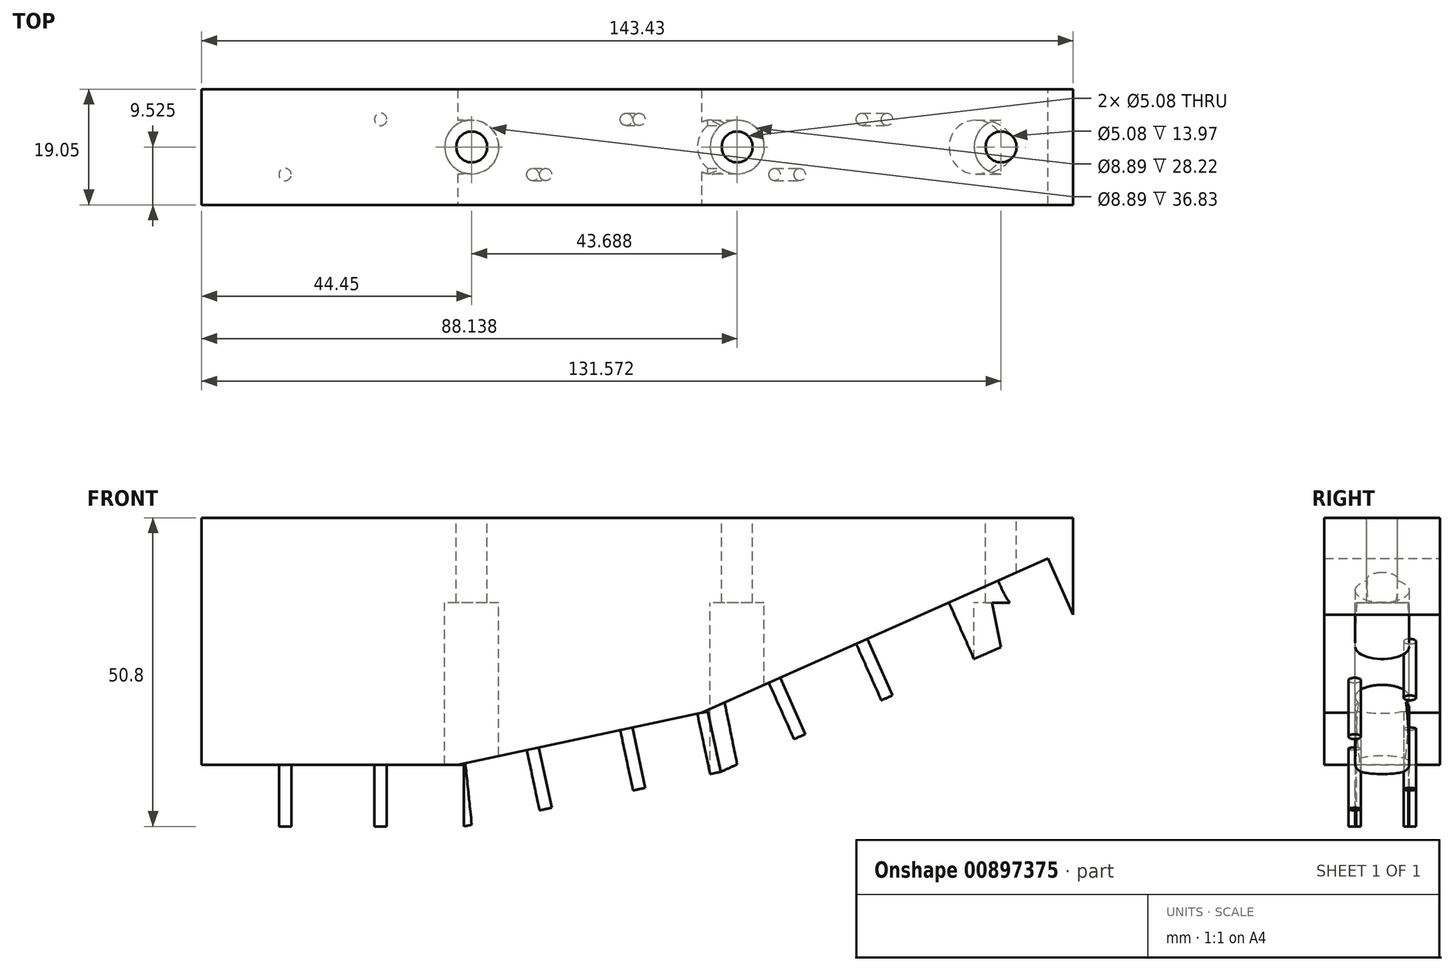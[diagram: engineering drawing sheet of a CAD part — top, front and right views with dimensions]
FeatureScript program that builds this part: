
annotation { "Feature Type Name" : "Feature", "Feature Type Description" : "" }
export const myFeature = defineFeature(function(context is Context, id is Id, definition is map)
    precondition{}
    {
        {
            var Q0;
            Q0=qCreatedBy(makeId("Front.planeOp"),FACE);
            var sketch = newSketch(context, id + "F0", { "sketchPlane" : qUnion([Q0])});
            skLineSegment(sketch, "E0.left", {"start": v(6.35, 57.15) * mm, "end": v(6.35, 6.35) * mm});
            skLineSegment(sketch, "E1", {"start": v(6.35, 6.35) * mm, "end": v(49.53, 6.35) * mm});
            skLineSegment(sketch, "E2", {"start": v(49.53, 6.35) * mm, "end": v(91.77, 15.33) * mm});
            skLineSegment(sketch, "E3", {"start": v(91.77, 15.33) * mm, "end": v(149.78, 41.16) * mm});
            skLineSegment(sketch, "E4", {"start": v(149.78, 41.16) * mm, "end": v(149.78, 57.15) * mm});
            skLineSegment(sketch, "E5", {"start": v(6.35, 57.15) * mm, "end": v(149.8, 57.15) * mm});
            skSolve(sketch);
        }
        {
            var Q0;
            {var subQ0=sQuery(id+"F0.wireOp",EDGE,"E0.left");Q0=makeQuery(id+"F0.imprint","IMPRINT",FACE,{"disambiguationData":[TD([[makeQuery(id+"F0.imprint","IMPRINT",EDGE,{"derivedFrom":subQ0}),1.0]])]});}
            extrude(context, id + "F1", {"entities" : qUnion([Q0]), "depth" : 19.05 * mm, "offsetDistance" : 25.4 * mm});
        }
        {
            var Q0;
            Q0=makeQuery(id+"F1.opExtrude","SWEPT_FACE",FACE,{"disambiguationData":[OSD([sQuery(id+"F0.wireOp",EDGE,"E5")])]});
            var sketch = newSketch(context, id + "F2", { "sketchPlane" : qUnion([Q0])});
            skLineSegment(sketch, "E6", {"start": v(50.8, 21.95) * mm, "end": v(50.8, -45.54) * mm, "construction": true});
            skLineSegment(sketch, "E7", {"start": v(94.49, 24.88) * mm, "end": v(94.49, -40.3) * mm, "construction": true});
            skLineSegment(sketch, "E8", {"start": v(137.92, 28.66) * mm, "end": v(137.92, -40.3) * mm, "construction": true});
            skLineSegment(sketch, "E9", {"start": v(-7.3, -9.53) * mm, "end": v(174, -9.53) * mm, "construction": true});
            skPoint(sketch, "E9.startSnap0", {"position": v(6.35, -9.53) * mm});
            skCircle(sketch, "E10", {"center": v(50.8, -9.53) * mm, "radius": 4.45 * mm});
            skCircle(sketch, "E11", {"center": v(94.49, -9.53) * mm, "radius": 4.45 * mm});
            skCircle(sketch, "E12", {"center": v(137.92, -9.53) * mm, "radius": 4.45 * mm});
            skCircle(sketch, "E13", {"center": v(50.8, -9.53) * mm, "radius": 2.54 * mm});
            skCircle(sketch, "E14", {"center": v(94.49, -9.53) * mm, "radius": 2.54 * mm});
            skCircle(sketch, "E15", {"center": v(137.92, -9.53) * mm, "radius": 2.54 * mm});
            skSolve(sketch);
        }
        {
            var Q0;
            Q0=makeQuery(id+"F2.imprint","IMPRINT",FACE,{"disambiguationData":[TD([[makeQuery(id+"F2.imprint","IMPRINT",EDGE,{"derivedFrom":sQuery(id+"F2.wireOp",EDGE,"E13")}),1.0]])]});
            var Q1;
            Q1=makeQuery(id+"F2.imprint","IMPRINT",FACE,{"disambiguationData":[TD([[makeQuery(id+"F2.imprint","IMPRINT",EDGE,{"derivedFrom":sQuery(id+"F2.wireOp",EDGE,"E14")}),1.0]])]});
            var Q2;
            Q2=makeQuery(id+"F2.imprint","IMPRINT",FACE,{"disambiguationData":[TD([[makeQuery(id+"F2.imprint","IMPRINT",EDGE,{"derivedFrom":sQuery(id+"F2.wireOp",EDGE,"E15")}),1.0]])]});
            extrude(context, id + "F3", {"entities" : qUnion([Q0, Q1, Q2]), "operationType" : NewBodyOperationType.REMOVE, "endBound" : BoundingType.THROUGH_ALL, "oppositeDirection" : true, "depth" : 25.4 * mm, "offsetDistance" : 25.4 * mm});
        }
        {
            var Q0;
            Q0=makeQuery(id+"F2.imprint","IMPRINT",FACE,{"disambiguationData":[TD([[makeQuery(id+"F2.imprint","IMPRINT",EDGE,{"derivedFrom":sQuery(id+"F2.wireOp",EDGE,"E10")}),1.0]])]});
            var Q1;
            Q1=makeQuery(id+"F2.imprint","IMPRINT",FACE,{"disambiguationData":[TD([[makeQuery(id+"F2.imprint","IMPRINT",EDGE,{"derivedFrom":sQuery(id+"F2.wireOp",EDGE,"E11")}),1.0]])]});
            var Q2;
            Q2=makeQuery(id+"F2.imprint","IMPRINT",FACE,{"disambiguationData":[TD([[makeQuery(id+"F2.imprint","IMPRINT",EDGE,{"derivedFrom":sQuery(id+"F2.wireOp",EDGE,"E12")}),1.0]])]});
            extrude(context, id + "F4", {"entities" : qUnion([Q0, Q1, Q2]), "operationType" : NewBodyOperationType.REMOVE, "oppositeDirection" : true, "depth" : 54.36 * mm, "offsetDistance" : 25.4 * mm, "hasSecondDirection" : true, "secondDirectionOppositeDirection" : true, "secondDirectionDepth" : 13.97 * mm});
        }
        {
            var Q0;
            Q0=makeQuery(id+"F1.opExtrude","SWEPT_FACE",FACE,{"disambiguationData":[OSD([sQuery(id+"F0.wireOp",EDGE,"E1")])]});
            var sketch = newSketch(context, id + "F5", { "sketchPlane" : qUnion([Q0])});
            skLineSegment(sketch, "E16", {"start": v(27.94, 21.39) * mm, "end": v(27.94, -3.77) * mm, "construction": true});
            skPoint(sketch, "E16.startSnap0", {"position": v(27.94, 19.05) * mm});
            skLineSegment(sketch, "E17", {"start": v(2.63, 9.53) * mm, "end": v(172.55, 9.53) * mm, "construction": true});
            skPoint(sketch, "E17.startSnap0", {"position": v(6.35, 9.53) * mm});
            skCircle(sketch, "E18", {"center": v(27.94, 9.53) * mm, "radius": 9.08 * mm});
            skLineSegment(sketch, "E19", {"start": v(27.94, -11.85) * mm, "end": v(27.94, 27.97) * mm, "construction": true});
            skLineSegment(sketch, "E20", {"start": v(5.3, 9.53) * mm, "end": v(51, 9.53) * mm, "construction": true});
            skLineSegment(sketch, "E21", {"start": v(20.08, 14.07) * mm, "end": v(50.17, -3.3) * mm, "construction": true});
            skCircle(sketch, "E22", {"center": v(20.08, 14.07) * mm, "radius": 1.02 * mm});
            skCircle(sketch, "E23", {"center": v(35.8, 4.98) * mm, "radius": 1.02 * mm});
            skSolve(sketch);
        }
        {
            var Q0;
            {var subQ0=sQuery(id+"F5.wireOp",EDGE,"E22");var subQ1=sQuery(id+"F5.wireOp",EDGE,"E18");var subQ2=makeQuery(id+"F5.imprint","INTERSECT",VERTEX,{"disambiguationData":[OD(0.0)],"derivedFrom":[subQ1,subQ0]});Q0=makeQuery(id+"F5.imprint","IMPRINT",FACE,{"disambiguationData":[TD([[makeQuery(id+"F5.imprint","IMPRINT",EDGE,{"disambiguationData":[TD([[subQ2,1.0]])],"derivedFrom":subQ1}),-1.0]])]});}
            var Q1;
            {var subQ0=sQuery(id+"F5.wireOp",EDGE,"E22");var subQ1=sQuery(id+"F5.wireOp",EDGE,"E18");var subQ2=makeQuery(id+"F5.imprint","INTERSECT",VERTEX,{"disambiguationData":[OD(0.0)],"derivedFrom":[subQ1,subQ0]});Q1=makeQuery(id+"F5.imprint","IMPRINT",FACE,{"disambiguationData":[TD([[makeQuery(id+"F5.imprint","IMPRINT",EDGE,{"disambiguationData":[TD([[subQ2,1.0]])],"derivedFrom":subQ1}),1.0]])]});}
            var Q2;
            {var subQ0=sQuery(id+"F5.wireOp",EDGE,"E23");var subQ1=sQuery(id+"F5.wireOp",EDGE,"E18");var subQ2=makeQuery(id+"F5.imprint","INTERSECT",VERTEX,{"disambiguationData":[OD(0.0)],"derivedFrom":[subQ1,subQ0]});Q2=makeQuery(id+"F5.imprint","IMPRINT",FACE,{"disambiguationData":[TD([[makeQuery(id+"F5.imprint","IMPRINT",EDGE,{"disambiguationData":[TD([[subQ2,-1.0]])],"derivedFrom":subQ1}),1.0]])]});}
            var Q3;
            {var subQ0=sQuery(id+"F5.wireOp",EDGE,"E23");var subQ1=sQuery(id+"F5.wireOp",EDGE,"E18");var subQ2=makeQuery(id+"F5.imprint","INTERSECT",VERTEX,{"disambiguationData":[OD(0.0)],"derivedFrom":[subQ1,subQ0]});Q3=makeQuery(id+"F5.imprint","IMPRINT",FACE,{"disambiguationData":[TD([[makeQuery(id+"F5.imprint","IMPRINT",EDGE,{"disambiguationData":[TD([[subQ2,-1.0]])],"derivedFrom":subQ1}),-1.0]])]});}
            extrude(context, id + "F6", {"entities" : qUnion([Q0, Q1, Q2, Q3]), "operationType" : NewBodyOperationType.REMOVE, "oppositeDirection" : true, "depth" : 10.16 * mm, "offsetDistance" : 25.4 * mm});
        }
        {
            var Q0;
            Q0=makeQuery(id+"F1.opExtrude","SWEPT_FACE",FACE,{"disambiguationData":[OSD([sQuery(id+"F0.wireOp",EDGE,"E2")])]});
            var sketch = newSketch(context, id + "F7", { "sketchPlane" : qUnion([Q0])});
            skLineSegment(sketch, "E24", {"start": v(71.36, 24.49) * mm, "end": v(71.36, -6.6) * mm, "construction": true});
            skPoint(sketch, "E24.startSnap0", {"position": v(71.36, 19.05) * mm});
            skLineSegment(sketch, "E25", {"start": v(91.19, 9.53) * mm, "end": v(55.61, 9.53) * mm, "construction": true});
            skLineSegment(sketch, "E26", {"start": v(71.36, 21.39) * mm, "end": v(71.36, -3.77) * mm, "construction": true});
            skPoint(sketch, "E27.startSnap0", {"position": v(49.77, 9.53) * mm});
            skCircle(sketch, "E28", {"center": v(71.36, 9.53) * mm, "radius": 9.08 * mm});
            skLineSegment(sketch, "E29", {"start": v(71.36, -11.85) * mm, "end": v(71.36, 27.97) * mm, "construction": true});
            skLineSegment(sketch, "E30", {"start": v(48.73, 9.53) * mm, "end": v(94.42, 9.53) * mm, "construction": true});
            skLineSegment(sketch, "E31", {"start": v(63.5, 14.07) * mm, "end": v(93.59, -3.3) * mm, "construction": true});
            skCircle(sketch, "E32", {"center": v(63.5, 14.07) * mm, "radius": 1.02 * mm});
            skCircle(sketch, "E33", {"center": v(79.23, 4.98) * mm, "radius": 1.02 * mm});
            skSolve(sketch);
        }
        {
            var Q0;
            {var subQ0=sQuery(id+"F7.wireOp",EDGE,"E32");var subQ1=sQuery(id+"F7.wireOp",EDGE,"E28");var subQ2=makeQuery(id+"F7.imprint","INTERSECT",VERTEX,{"disambiguationData":[OD(0.0)],"derivedFrom":[subQ1,subQ0]});Q0=makeQuery(id+"F7.imprint","IMPRINT",FACE,{"disambiguationData":[TD([[makeQuery(id+"F7.imprint","IMPRINT",EDGE,{"disambiguationData":[TD([[subQ2,1.0]])],"derivedFrom":subQ1}),1.0]])]});}
            var Q1;
            {var subQ0=sQuery(id+"F7.wireOp",EDGE,"E32");var subQ1=sQuery(id+"F7.wireOp",EDGE,"E28");var subQ2=makeQuery(id+"F7.imprint","INTERSECT",VERTEX,{"disambiguationData":[OD(0.0)],"derivedFrom":[subQ1,subQ0]});Q1=makeQuery(id+"F7.imprint","IMPRINT",FACE,{"disambiguationData":[TD([[makeQuery(id+"F7.imprint","IMPRINT",EDGE,{"disambiguationData":[TD([[subQ2,1.0]])],"derivedFrom":subQ1}),-1.0]])]});}
            var Q2;
            {var subQ0=sQuery(id+"F7.wireOp",EDGE,"E33");var subQ1=sQuery(id+"F7.wireOp",EDGE,"E28");var subQ2=makeQuery(id+"F7.imprint","INTERSECT",VERTEX,{"disambiguationData":[OD(0.0)],"derivedFrom":[subQ1,subQ0]});Q2=makeQuery(id+"F7.imprint","IMPRINT",FACE,{"disambiguationData":[TD([[makeQuery(id+"F7.imprint","IMPRINT",EDGE,{"disambiguationData":[TD([[subQ2,-1.0]])],"derivedFrom":subQ1}),1.0]])]});}
            var Q3;
            {var subQ0=sQuery(id+"F7.wireOp",EDGE,"E33");var subQ1=sQuery(id+"F7.wireOp",EDGE,"E28");var subQ2=makeQuery(id+"F7.imprint","INTERSECT",VERTEX,{"disambiguationData":[OD(0.0)],"derivedFrom":[subQ1,subQ0]});Q3=makeQuery(id+"F7.imprint","IMPRINT",FACE,{"disambiguationData":[TD([[makeQuery(id+"F7.imprint","IMPRINT",EDGE,{"disambiguationData":[TD([[subQ2,-1.0]])],"derivedFrom":subQ1}),-1.0]])]});}
            extrude(context, id + "F8", {"entities" : qUnion([Q0, Q1, Q2, Q3]), "operationType" : NewBodyOperationType.REMOVE, "oppositeDirection" : true, "depth" : 10.16 * mm, "offsetDistance" : 25.4 * mm});
        }
        {
            var Q0;
            Q0=makeQuery(id+"F1.opExtrude","SWEPT_FACE",FACE,{"disambiguationData":[OSD([sQuery(id+"F0.wireOp",EDGE,"E3")])]});
            var sketch = newSketch(context, id + "F9", { "sketchPlane" : qUnion([Q0])});
            skLineSegment(sketch, "E34", {"start": v(112.17, 26.3) * mm, "end": v(112.17, -8.5) * mm, "construction": true});
            skLineSegment(sketch, "E35", {"start": v(153.57, 9.53) * mm, "end": v(76.28, 9.53) * mm, "construction": true});
            skPoint(sketch, "E35.endSnap0", {"position": v(88.18, 9.53) * mm});
            skLineSegment(sketch, "E36", {"start": v(112.17, 21.39) * mm, "end": v(112.17, -3.77) * mm, "construction": true});
            skPoint(sketch, "E36.startSnap0", {"position": v(112.17, 19.05) * mm});
            skPoint(sketch, "E37.startSnap0", {"position": v(90.58, 9.52) * mm});
            skCircle(sketch, "E38", {"center": v(112.17, 9.53) * mm, "radius": 9.08 * mm});
            skLineSegment(sketch, "E39", {"start": v(112.17, -11.85) * mm, "end": v(112.17, 27.97) * mm, "construction": true});
            skLineSegment(sketch, "E40", {"start": v(89.53, 9.53) * mm, "end": v(135.23, 9.53) * mm, "construction": true});
            skLineSegment(sketch, "E41", {"start": v(104.3, 14.07) * mm, "end": v(134.4, -3.3) * mm, "construction": true});
            skCircle(sketch, "E42", {"center": v(104.3, 14.07) * mm, "radius": 1.02 * mm});
            skCircle(sketch, "E43", {"center": v(120.03, 4.98) * mm, "radius": 1.02 * mm});
            skSolve(sketch);
        }
        {
            var Q0;
            {var subQ0=sQuery(id+"F9.wireOp",EDGE,"E42");var subQ1=sQuery(id+"F9.wireOp",EDGE,"E38");var subQ2=makeQuery(id+"F9.imprint","INTERSECT",VERTEX,{"disambiguationData":[OD(0.0)],"derivedFrom":[subQ1,subQ0]});Q0=makeQuery(id+"F9.imprint","IMPRINT",FACE,{"disambiguationData":[TD([[makeQuery(id+"F9.imprint","IMPRINT",EDGE,{"disambiguationData":[TD([[subQ2,1.0]])],"derivedFrom":subQ1}),1.0]])]});}
            var Q1;
            {var subQ0=sQuery(id+"F9.wireOp",EDGE,"E42");var subQ1=sQuery(id+"F9.wireOp",EDGE,"E38");var subQ2=makeQuery(id+"F9.imprint","INTERSECT",VERTEX,{"disambiguationData":[OD(0.0)],"derivedFrom":[subQ1,subQ0]});Q1=makeQuery(id+"F9.imprint","IMPRINT",FACE,{"disambiguationData":[TD([[makeQuery(id+"F9.imprint","IMPRINT",EDGE,{"disambiguationData":[TD([[subQ2,1.0]])],"derivedFrom":subQ1}),-1.0]])]});}
            var Q2;
            {var subQ0=sQuery(id+"F9.wireOp",EDGE,"E43");var subQ1=sQuery(id+"F9.wireOp",EDGE,"E38");var subQ2=makeQuery(id+"F9.imprint","INTERSECT",VERTEX,{"disambiguationData":[OD(0.0)],"derivedFrom":[subQ1,subQ0]});Q2=makeQuery(id+"F9.imprint","IMPRINT",FACE,{"disambiguationData":[TD([[makeQuery(id+"F9.imprint","IMPRINT",EDGE,{"disambiguationData":[TD([[subQ2,-1.0]])],"derivedFrom":subQ1}),1.0]])]});}
            var Q3;
            {var subQ0=sQuery(id+"F9.wireOp",EDGE,"E43");var subQ1=sQuery(id+"F9.wireOp",EDGE,"E38");var subQ2=makeQuery(id+"F9.imprint","INTERSECT",VERTEX,{"disambiguationData":[OD(0.0)],"derivedFrom":[subQ1,subQ0]});Q3=makeQuery(id+"F9.imprint","IMPRINT",FACE,{"disambiguationData":[TD([[makeQuery(id+"F9.imprint","IMPRINT",EDGE,{"disambiguationData":[TD([[subQ2,-1.0]])],"derivedFrom":subQ1}),-1.0]])]});}
            extrude(context, id + "F10", {"entities" : qUnion([Q0, Q1, Q2, Q3]), "operationType" : NewBodyOperationType.REMOVE, "oppositeDirection" : true, "depth" : 10.16 * mm, "offsetDistance" : 25.4 * mm});
        }
    });
